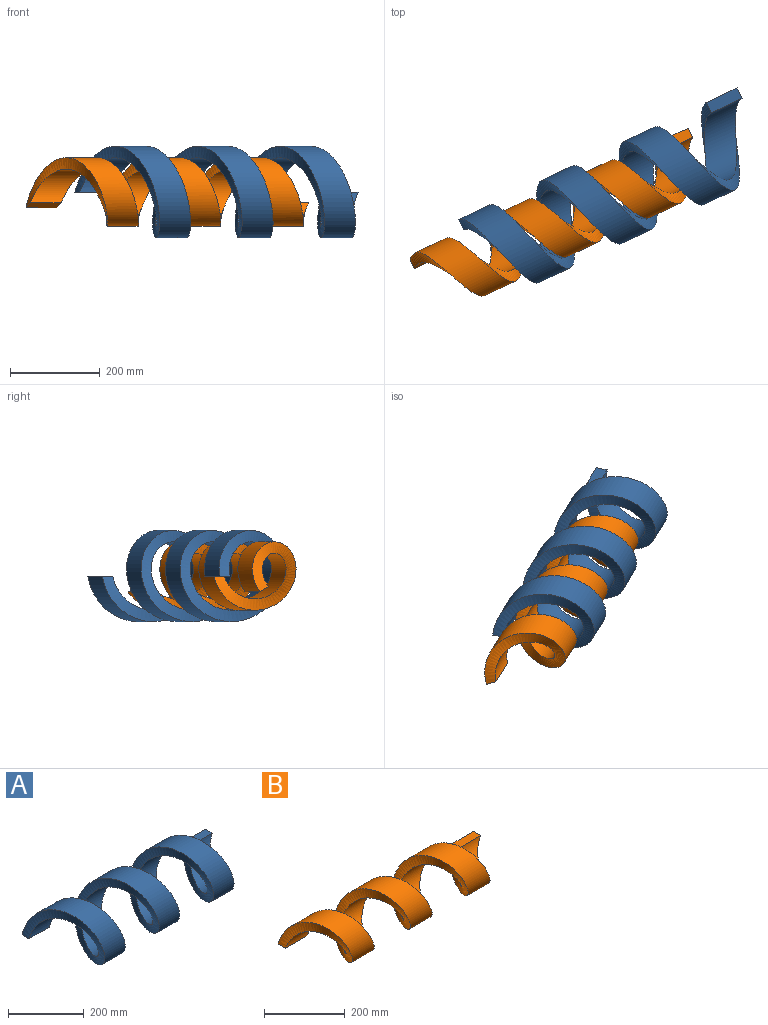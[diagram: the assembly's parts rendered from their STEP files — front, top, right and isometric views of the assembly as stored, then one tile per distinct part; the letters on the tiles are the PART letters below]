
ASSEMBLY  parts=2 mates=1
PART A: 6 faces, bbox 685.8x203.2x203.2 mm
  f0: cylinder r=101.6mm len=685.8mm, axis (1,0,0), area 145931.8mm2, adj f1,f2,f3,f4
  f1: bspline ~609.6x203.2mm, area 45298.6mm2, adj f0,f3,f4,f5
  f2: bspline ~609.6x203.2mm, area 45298.6mm2, adj f0,f3,f4,f5
  f3: plane 76.2x25.4mm, normal (0,0,1), area 1935.5mm2, adj f0,f1,f2,f5
  f4: plane 76.2x25.4mm, normal (0,0,-1), area 1935.5mm2, adj f0,f1,f2,f5
  f5: cylinder r=76.2mm len=685.8mm, axis (1,0,0), area 109448.8mm2, adj f1,f2,f3,f4
PART B: 6 faces, bbox 685.8x203.2x203.2 mm
  f0: plane 76.2x25.4mm, normal (0,0,-1), area 1935.5mm2, adj f2,f3,f4,f5
  f1: plane 76.2x25.4mm, normal (0,0,1), area 1935.5mm2, adj f2,f3,f4,f5
  f2: bspline ~609.6x203.2mm, area 34147.6mm2, adj f0,f1,f3,f5
  f3: cylinder r=50.8mm len=685.8mm, axis (1,0,0), area 72965.9mm2, adj f0,f1,f2,f4
  f4: bspline ~609.6x203.2mm, area 34147.6mm2, adj f0,f1,f3,f5
  f5: cylinder r=76.2mm len=685.8mm, axis (1,0,0), area 109448.8mm2, adj f0,f1,f2,f4
PLACE A rot(axis=(0,0,1),25.3deg) t=(44.32,-31.59,0)mm fixed
PLACE B rot(axis=(-0.73,-0.16,0.66),37.4deg) t=(-76.52,-95.19,-23.64)mm
MATE cylindrical B.f3 <-> A.f0  axis (0.9,0.43,0) through (218.25,-5.55,0)mm
